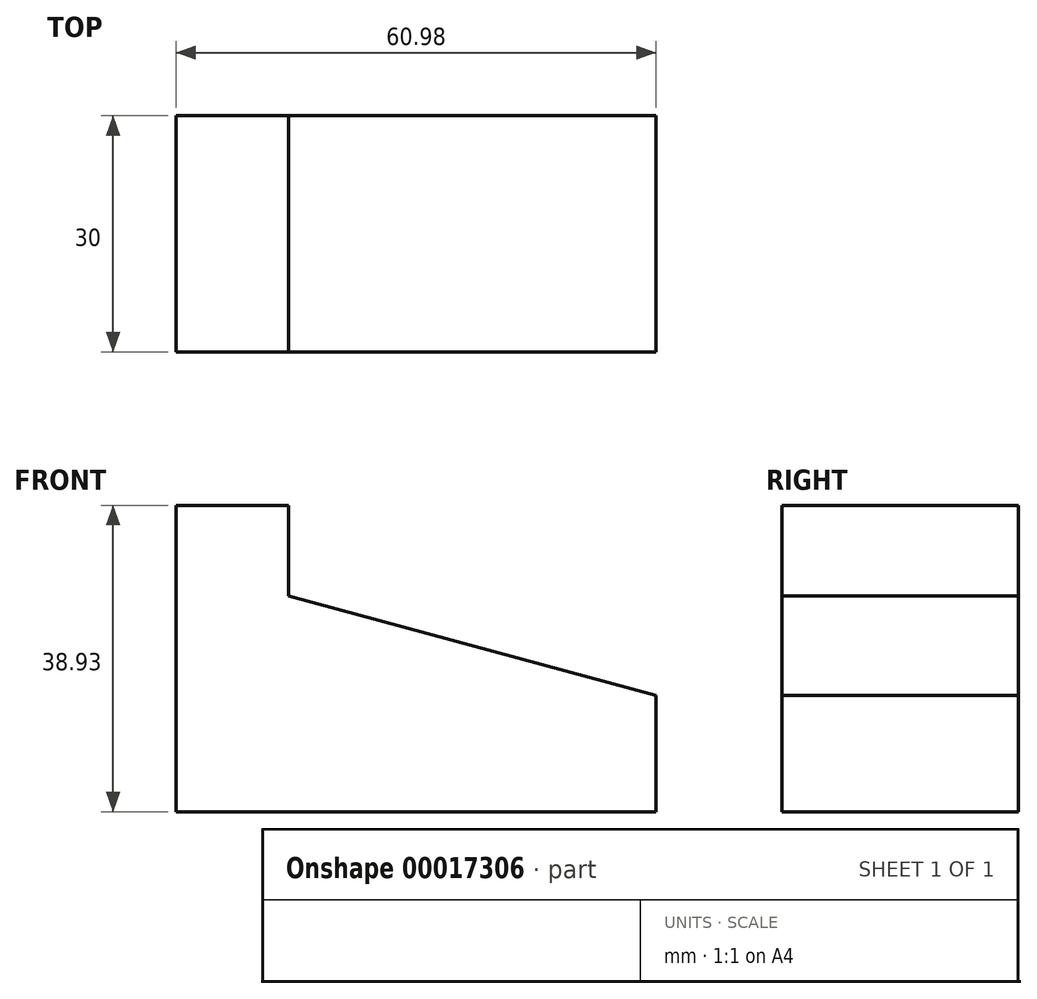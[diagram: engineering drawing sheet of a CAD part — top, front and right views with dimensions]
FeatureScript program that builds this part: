
annotation { "Feature Type Name" : "Feature", "Feature Type Description" : "" }
export const myFeature = defineFeature(function(context is Context, id is Id, definition is map)
    precondition{}
    {
        {
            var Q0;
            Q0=qCreatedBy(makeId("Front.planeOp"),FACE);
            var sketch = newSketch(context, id + "F0", { "sketchPlane" : qUnion([Q0])});
            skLineSegment(sketch, "E0", {"start": v(-42.1, 24.13) * mm, "end": v(-42.1, -14.8) * mm});
            skLineSegment(sketch, "E1", {"start": v(-42.1, 24.13) * mm, "end": v(-27.8, 24.13) * mm});
            skLineSegment(sketch, "E2", {"start": v(-27.8, 24.13) * mm, "end": v(-27.8, 12.61) * mm});
            skLineSegment(sketch, "E3", {"start": v(-42.1, -14.8) * mm, "end": v(18.87, -14.8) * mm});
            skLineSegment(sketch, "E4", {"start": v(18.87, -14.8) * mm, "end": v(18.87, 0) * mm});
            skLineSegment(sketch, "E5", {"start": v(-27.8, 12.61) * mm, "end": v(18.87, 0) * mm});
            skSolve(sketch);
        }
        {
            var Q0;
            Q0=makeQuery(id+"F0.imprint","IMPRINT",FACE,{"disambiguationData":[TD([[makeQuery(id+"F0.imprint","IMPRINT",EDGE,{"derivedFrom":sQuery(id+"F0.wireOp",EDGE,"E0")}),1.0]])]});
            extrude(context, id + "F1", {"entities" : qUnion([Q0]), "depth" : 30 * mm});
        }
    });
